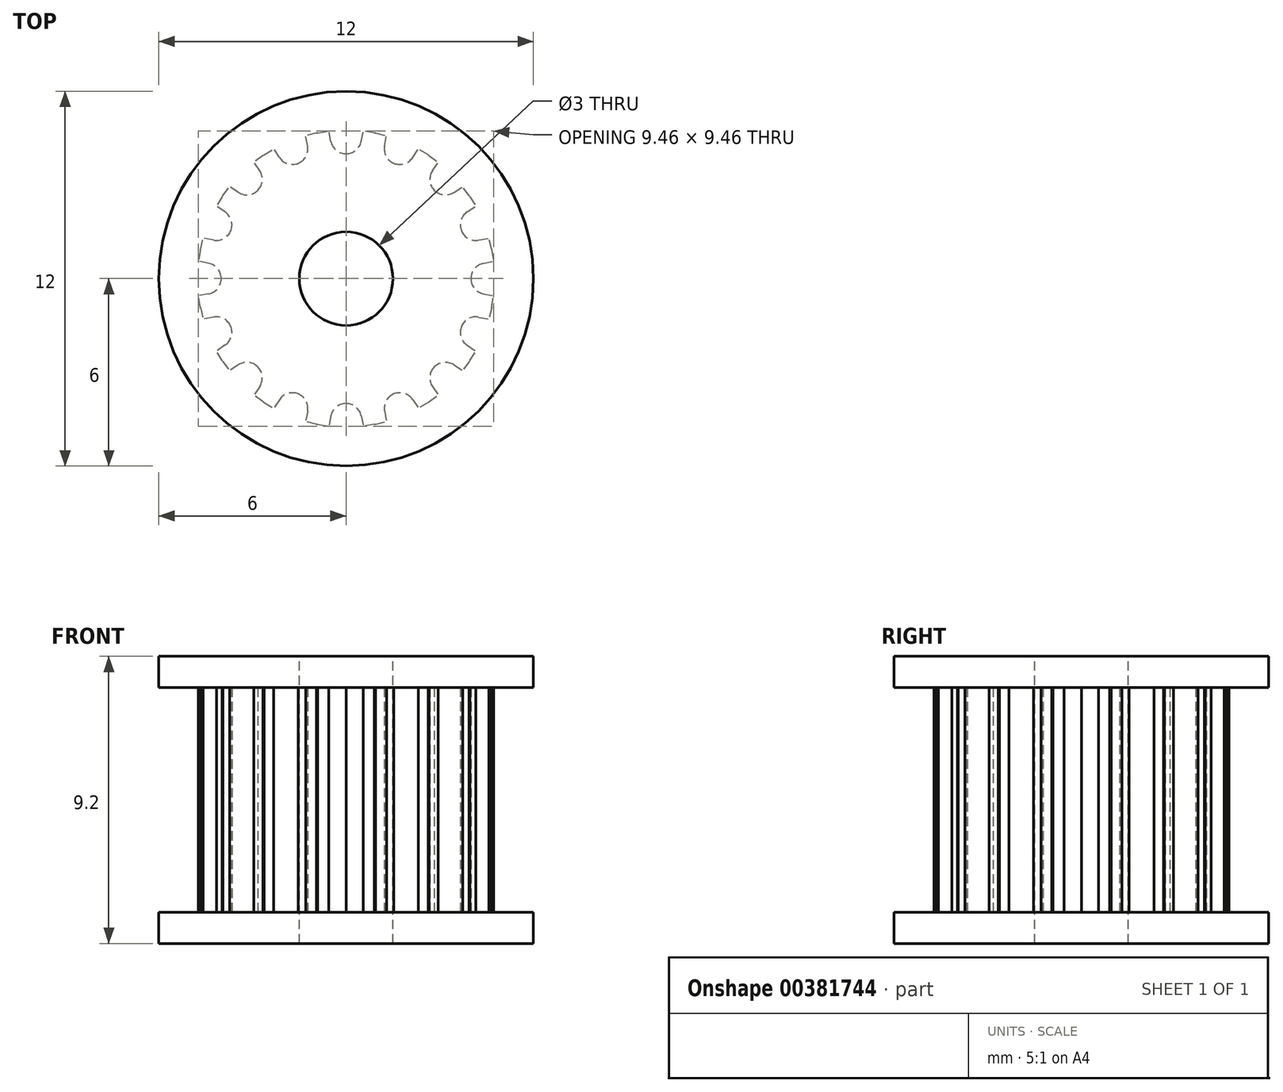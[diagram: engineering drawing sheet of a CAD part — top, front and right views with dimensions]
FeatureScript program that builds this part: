
annotation { "Feature Type Name" : "Feature", "Feature Type Description" : "" }
export const myFeature = defineFeature(function(context is Context, id is Id, definition is map)
    precondition{}
    {
        {
            var Q0;
            Q0=qCreatedBy(makeId("Top.planeOp"),FACE);
            var sketch = newSketch(context, id + "F0", { "sketchPlane" : qUnion([Q0])});
            skCircle(sketch, "E0", {"center": v(0, 0) * mm, "radius": 4 * mm, "construction": true});
            skLineSegment(sketch, "E1", {"start": v(0, 0) * mm, "end": v(0, 4) * mm, "construction": true});
            skLineSegment(sketch, "E2", {"start": v(0, 0) * mm, "end": v(-0.95, 4.66) * mm});
            skCircle(sketch, "E3", {"center": v(0, 0) * mm, "radius": 4.76 * mm, "construction": true});
            skLineSegment(sketch, "E4", {"start": v(0, 4) * mm, "end": v(0, 4) * mm});
            skLineSegment(sketch, "E5.0", {"start": v(-0.49, 4.4) * mm, "end": v(-0.55, 4.73) * mm});
            skLineSegment(sketch, "E6.MirrorCS", {"start": v(0.4, 4) * mm, "end": v(0.55, 4.73) * mm});
            skPoint(sketch, "E7.newPointB", {"position": v(-0.55, 4.73) * mm});
            skArc(sketch, "E7.filletArc", {"start": v(-0.49, 4.4) * mm, "mid": v(-0.31, 4.11) * mm, "end": v(0, 4) * mm});
            skLineSegment(sketch, "E8", {"start": v(-0.95, 4.66) * mm, "end": v(-0.55, 4.73) * mm});
            skPoint(sketch, "E9.MirrorCS.end.orphan", {"position": v(0.95, 4.66) * mm});
            skLineSegment(sketch, "E10.trimOffspring", {"start": v(0.55, 4.73) * mm, "end": v(0.55, 4.73) * mm});
            skLineSegment(sketch, "E11.MirrorCS", {"start": v(0, 0) * mm, "end": v(0.95, 4.66) * mm});
            skLineSegment(sketch, "E12.MirrorCS", {"start": v(0.49, 4.4) * mm, "end": v(0.55, 4.73) * mm});
            skArc(sketch, "E13.MirrorCS", {"start": v(0.49, 4.4) * mm, "mid": v(0.31, 4.11) * mm, "end": v(0, 4) * mm});
            skLineSegment(sketch, "E14.MirrorCS", {"start": v(0.95, 4.66) * mm, "end": v(0.55, 4.73) * mm});
            skSolve(sketch);
        }
        {
            var Q0;
            Q0=makeQuery(id+"F0.imprint","IMPRINT",FACE,{"disambiguationData":[TD([[makeQuery(id+"F0.imprint","IMPRINT",EDGE,{"derivedFrom":sQuery(id+"F0.wireOp",EDGE,"E2")}),-1.0]])]});
            extrude(context, id + "F1", {"entities" : qUnion([Q0]), "flatOperationType" : FlatOperationType.REMOVE, "endBound" : BoundingType.SYMMETRIC, "offsetDistance" : 25 * mm, "depth" : 7.2 * mm, "domain" : OperationDomain.MODEL});
        }
        {
            var Q0;
            Q0=makeQuery(id+"F1.opExtrude","SWEPT_BODY",BODY,{"disambiguationData":[OSD([sQuery(id+"F0.wireOp",EDGE,"E2"),sQuery(id+"F0.wireOp",EDGE,"E4"),sQuery(id+"F0.wireOp",EDGE,"E5.0"),sQuery(id+"F0.wireOp",EDGE,"E7.filletArc"),sQuery(id+"F0.wireOp",EDGE,"E8"),sQuery(id+"F0.wireOp",EDGE,"E11.MirrorCS"),sQuery(id+"F0.wireOp",EDGE,"E12.MirrorCS"),sQuery(id+"F0.wireOp",EDGE,"E13.MirrorCS"),sQuery(id+"F0.wireOp",EDGE,"E4"),sQuery(id+"F0.wireOp",EDGE,"E14.MirrorCS")])]});
            var Q1;
            Q1=makeQuery(id+"F1.opExtrude","SWEPT_EDGE",EDGE,{"disambiguationData":[OSD([sQuery(id+"F0.wireOp",EDGE,"E2"),sQuery(id+"F0.wireOp",EDGE,"E11.MirrorCS")])]});
            circularPattern(context, id + "F2", {"operationType" : NewBodyOperationType.ADD, "entities" : qUnion([Q0]), "axis" : qUnion([Q1]), "angle" : 360 * degree, "instanceCount" : 16, "equalSpace" : true});
        }
        {
            var Q0;
            {var subQ0=makeQuery(id+"F1.opExtrude","CAP_FACE",FACE,{"disambiguationData":[OSD([sQuery(id+"F0.wireOp",EDGE,"E2"),sQuery(id+"F0.wireOp",EDGE,"E4"),sQuery(id+"F0.wireOp",EDGE,"E5.0"),sQuery(id+"F0.wireOp",EDGE,"E7.filletArc"),sQuery(id+"F0.wireOp",EDGE,"E8"),sQuery(id+"F0.wireOp",EDGE,"E11.MirrorCS"),sQuery(id+"F0.wireOp",EDGE,"E12.MirrorCS"),sQuery(id+"F0.wireOp",EDGE,"E13.MirrorCS"),sQuery(id+"F0.wireOp",EDGE,"E4"),sQuery(id+"F0.wireOp",EDGE,"E14.MirrorCS")])],"isStart":true});Q0=makeQuery(id+"F2.boolean.opBoolean","MERGE",FACE,{"derivedFrom":[subQ0,makeQuery(id+"F2.opPattern","COPY",FACE,{"derivedFrom":subQ0,"instanceName":"1"}),makeQuery(id+"F2.opPattern","COPY",FACE,{"derivedFrom":subQ0,"instanceName":"2"}),makeQuery(id+"F2.opPattern","COPY",FACE,{"derivedFrom":subQ0,"instanceName":"3"}),makeQuery(id+"F2.opPattern","COPY",FACE,{"derivedFrom":subQ0,"instanceName":"4"}),makeQuery(id+"F2.opPattern","COPY",FACE,{"derivedFrom":subQ0,"instanceName":"5"}),makeQuery(id+"F2.opPattern","COPY",FACE,{"derivedFrom":subQ0,"instanceName":"6"}),makeQuery(id+"F2.opPattern","COPY",FACE,{"derivedFrom":subQ0,"instanceName":"7"}),makeQuery(id+"F2.opPattern","COPY",FACE,{"derivedFrom":subQ0,"instanceName":"8"}),makeQuery(id+"F2.opPattern","COPY",FACE,{"derivedFrom":subQ0,"instanceName":"9"}),makeQuery(id+"F2.opPattern","COPY",FACE,{"derivedFrom":subQ0,"instanceName":"10"}),makeQuery(id+"F2.opPattern","COPY",FACE,{"derivedFrom":subQ0,"instanceName":"11"}),makeQuery(id+"F2.opPattern","COPY",FACE,{"derivedFrom":subQ0,"instanceName":"12"}),makeQuery(id+"F2.opPattern","COPY",FACE,{"derivedFrom":subQ0,"instanceName":"13"}),makeQuery(id+"F2.opPattern","COPY",FACE,{"derivedFrom":subQ0,"instanceName":"14"}),makeQuery(id+"F2.opPattern","COPY",FACE,{"derivedFrom":subQ0,"instanceName":"15"}),makeQuery(id+"F2.opPattern","COPY",FACE,{"derivedFrom":subQ0,"instanceName":"16"}),makeQuery(id+"F2.opPattern","COPY",FACE,{"derivedFrom":subQ0,"instanceName":"17"}),makeQuery(id+"F2.opPattern","COPY",FACE,{"derivedFrom":subQ0,"instanceName":"18"}),makeQuery(id+"F2.opPattern","COPY",FACE,{"derivedFrom":subQ0,"instanceName":"19"})]});}
            var sketch = newSketch(context, id + "F3", { "sketchPlane" : qUnion([Q0])});
            skCircle(sketch, "E15", {"center": v(0, 0) * mm, "radius": 6 * mm});
            skSolve(sketch);
        }
        {
            var Q0;
            Q0=makeQuery(id+"F3.imprint","IMPRINT",FACE,{"disambiguationData":[TD([[makeQuery(id+"F3.imprint","IMPRINT",EDGE,{"derivedFrom":sQuery(id+"F3.wireOp",EDGE,"E15")}),1.0]])]});
            var Q1;
            {var subQ2=makeQuery(id+"F1.opExtrude","CAP_EDGE",EDGE,{"disambiguationData":[OSD([sQuery(id+"F0.wireOp",EDGE,"E5.0")])],"isStart":true});Q1=makeQuery(id+"F3.imprint","IMPRINT",FACE,{"disambiguationData":[TD([[makeQuery(id+"F3.imprint","IMPRINT",EDGE,{"derivedFrom":subQ2}),-1.0]])]});}
            extrude(context, id + "F4", {"entities" : qUnion([Q0, Q1]), "operationType" : NewBodyOperationType.ADD, "depth" : 1 * mm});
        }
        {
            var Q0;
            {var subQ0=makeQuery(id+"F1.opExtrude","CAP_FACE",FACE,{"disambiguationData":[OSD([sQuery(id+"F0.wireOp",EDGE,"E2"),sQuery(id+"F0.wireOp",EDGE,"E4"),sQuery(id+"F0.wireOp",EDGE,"E5.0"),sQuery(id+"F0.wireOp",EDGE,"E7.filletArc"),sQuery(id+"F0.wireOp",EDGE,"E8"),sQuery(id+"F0.wireOp",EDGE,"E11.MirrorCS"),sQuery(id+"F0.wireOp",EDGE,"E12.MirrorCS"),sQuery(id+"F0.wireOp",EDGE,"E13.MirrorCS"),sQuery(id+"F0.wireOp",EDGE,"E4"),sQuery(id+"F0.wireOp",EDGE,"E14.MirrorCS")])],"isStart":false});Q0=makeQuery(id+"F2.boolean.opBoolean","MERGE",FACE,{"derivedFrom":[subQ0,makeQuery(id+"F2.opPattern","COPY",FACE,{"derivedFrom":subQ0,"instanceName":"1"}),makeQuery(id+"F2.opPattern","COPY",FACE,{"derivedFrom":subQ0,"instanceName":"2"}),makeQuery(id+"F2.opPattern","COPY",FACE,{"derivedFrom":subQ0,"instanceName":"3"}),makeQuery(id+"F2.opPattern","COPY",FACE,{"derivedFrom":subQ0,"instanceName":"4"}),makeQuery(id+"F2.opPattern","COPY",FACE,{"derivedFrom":subQ0,"instanceName":"5"}),makeQuery(id+"F2.opPattern","COPY",FACE,{"derivedFrom":subQ0,"instanceName":"6"}),makeQuery(id+"F2.opPattern","COPY",FACE,{"derivedFrom":subQ0,"instanceName":"7"}),makeQuery(id+"F2.opPattern","COPY",FACE,{"derivedFrom":subQ0,"instanceName":"8"}),makeQuery(id+"F2.opPattern","COPY",FACE,{"derivedFrom":subQ0,"instanceName":"9"}),makeQuery(id+"F2.opPattern","COPY",FACE,{"derivedFrom":subQ0,"instanceName":"10"}),makeQuery(id+"F2.opPattern","COPY",FACE,{"derivedFrom":subQ0,"instanceName":"11"}),makeQuery(id+"F2.opPattern","COPY",FACE,{"derivedFrom":subQ0,"instanceName":"12"}),makeQuery(id+"F2.opPattern","COPY",FACE,{"derivedFrom":subQ0,"instanceName":"13"}),makeQuery(id+"F2.opPattern","COPY",FACE,{"derivedFrom":subQ0,"instanceName":"14"}),makeQuery(id+"F2.opPattern","COPY",FACE,{"derivedFrom":subQ0,"instanceName":"15"}),makeQuery(id+"F2.opPattern","COPY",FACE,{"derivedFrom":subQ0,"instanceName":"16"}),makeQuery(id+"F2.opPattern","COPY",FACE,{"derivedFrom":subQ0,"instanceName":"17"}),makeQuery(id+"F2.opPattern","COPY",FACE,{"derivedFrom":subQ0,"instanceName":"18"}),makeQuery(id+"F2.opPattern","COPY",FACE,{"derivedFrom":subQ0,"instanceName":"19"})]});}
            var sketch = newSketch(context, id + "F5", { "sketchPlane" : qUnion([Q0])});
            skCircle(sketch, "E16.0", {"center": v(0, 0) * mm, "radius": 6 * mm});
            skSolve(sketch);
        }
        {
            var Q0;
            Q0=makeQuery(id+"F5.imprint","IMPRINT",FACE,{"disambiguationData":[TD([[makeQuery(id+"F5.imprint","IMPRINT",EDGE,{"derivedFrom":sQuery(id+"F5.wireOp",EDGE,"E16.0")}),1.0]])]});
            var Q1;
            {var subQ3=makeQuery(id+"F1.opExtrude","CAP_EDGE",EDGE,{"disambiguationData":[OSD([sQuery(id+"F0.wireOp",EDGE,"E5.0")])],"isStart":false});Q1=makeQuery(id+"F5.imprint","IMPRINT",FACE,{"disambiguationData":[TD([[makeQuery(id+"F5.imprint","IMPRINT",EDGE,{"derivedFrom":subQ3}),1.0]])]});}
            extrude(context, id + "F6", {"entities" : qUnion([Q0, Q1]), "operationType" : NewBodyOperationType.ADD, "flatOperationType" : FlatOperationType.REMOVE, "offsetDistance" : 25 * mm, "depth" : 1 * mm, "domain" : OperationDomain.MODEL});
        }
        {
            var Q0;
            Q0=makeQuery(id+"F6.opExtrude","CAP_FACE",FACE,{"disambiguationData":[OSD([sQuery(id+"F5.wireOp",EDGE,"E16.0")])],"isStart":false});
            var sketch = newSketch(context, id + "F7", { "sketchPlane" : qUnion([Q0])});
            skPoint(sketch, "E17", {"position": v(0, 0) * mm});
            skSolve(sketch);
        }
        {
            var Q0;
            Q0=sQuery(id+"F7.wireOp",VERTEX,"E17");
            var Q1;
            Q1=makeQuery(id+"F1.opExtrude","SWEPT_BODY",BODY,{"disambiguationData":[OSD([sQuery(id+"F0.wireOp",EDGE,"E2"),sQuery(id+"F0.wireOp",EDGE,"E4"),sQuery(id+"F0.wireOp",EDGE,"E5.0"),sQuery(id+"F0.wireOp",EDGE,"E7.filletArc"),sQuery(id+"F0.wireOp",EDGE,"E8"),sQuery(id+"F0.wireOp",EDGE,"E11.MirrorCS"),sQuery(id+"F0.wireOp",EDGE,"E12.MirrorCS"),sQuery(id+"F0.wireOp",EDGE,"E13.MirrorCS"),sQuery(id+"F0.wireOp",EDGE,"E4"),sQuery(id+"F0.wireOp",EDGE,"E14.MirrorCS")])]});
            hole(context, id + "F8", {"style" : HoleStyle.SIMPLE, "holeDiameter" : 3 * mm, "endStyle" : HoleEndStyle.THROUGH, "locations" : qUnion([Q0]), "scope" : qUnion([Q1]), "majorDiameter" : 5 * mm, "tappedDepth" : 12 * mm, "tapClearance" : 3});
        }
    });
